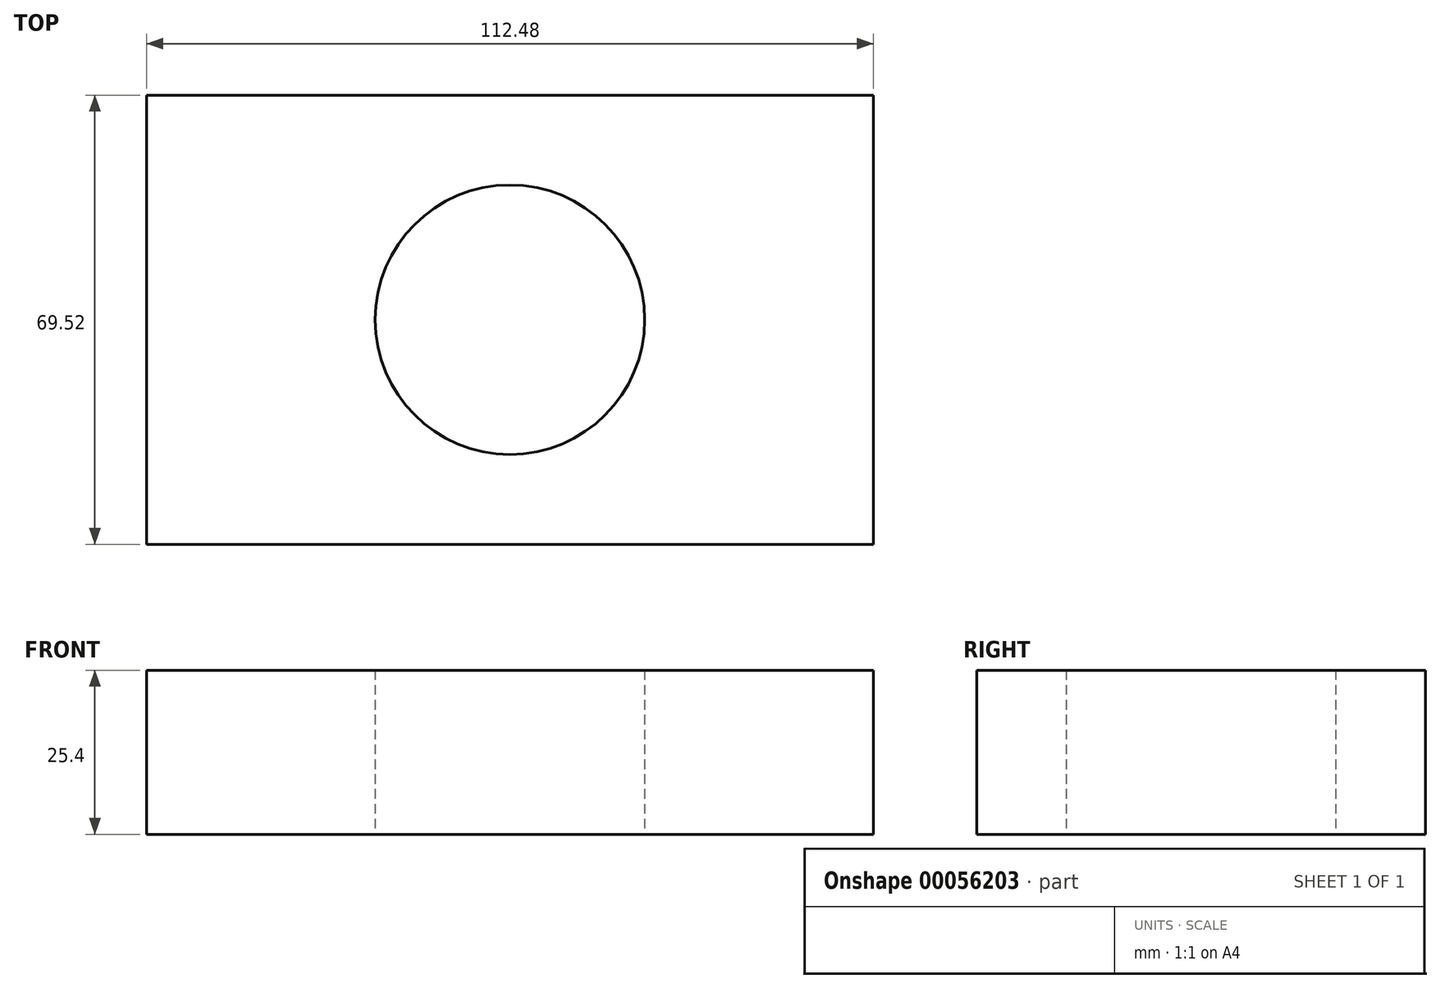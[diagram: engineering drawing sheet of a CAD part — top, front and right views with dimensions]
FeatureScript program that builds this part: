
annotation { "Feature Type Name" : "Feature", "Feature Type Description" : "" }
export const myFeature = defineFeature(function(context is Context, id is Id, definition is map)
    precondition{}
    {
        {
            var Q0;
            Q0=qCreatedBy(makeId("Top.planeOp"),FACE);
            var sketch = newSketch(context, id + "F0", { "sketchPlane" : qUnion([Q0])});
            skLineSegment(sketch, "E0.rect.bottom", {"start": v(-56.24, 34.76) * mm, "end": v(56.24, 34.76) * mm});
            skLineSegment(sketch, "E0.rect.top", {"start": v(-56.24, -34.76) * mm, "end": v(56.24, -34.76) * mm});
            skLineSegment(sketch, "E0.rect.left", {"start": v(-56.24, 34.76) * mm, "end": v(-56.24, -34.76) * mm});
            skLineSegment(sketch, "E0.rect.right", {"start": v(56.24, 34.76) * mm, "end": v(56.24, -34.76) * mm});
            skPoint(sketch, "E0.rect.middle", {"position": v(0, 0) * mm});
            skSolve(sketch);
        }
        {
            var Q0;
            Q0=qCreatedBy(makeId("Top.planeOp"),FACE);
            var sketch = newSketch(context, id + "F1", { "sketchPlane" : qUnion([Q0])});
            skCircle(sketch, "E1", {"center": v(0, 0) * mm, "radius": 20.85 * mm});
            skSolve(sketch);
        }
        {
            var Q0;
            Q0=makeQuery(id+"F0.imprint","IMPRINT",FACE,{"disambiguationData":[TD([[makeQuery(id+"F0.imprint","IMPRINT",EDGE,{"derivedFrom":sQuery(id+"F0.wireOp",EDGE,"E0.rect.bottom")}),-1.0]])]});
            var Q1;
            Q1=makeQuery(id+"F1.imprint","IMPRINT",FACE,{"disambiguationData":[TD([[makeQuery(id+"F1.imprint","IMPRINT",EDGE,{"derivedFrom":sQuery(id+"F1.wireOp",EDGE,"E1")}),1.0]])]});
            extrude(context, id + "F2", {"entities" : qUnion([Q0, Q1]), "depth" : 25.4 * mm});
        }
    });
